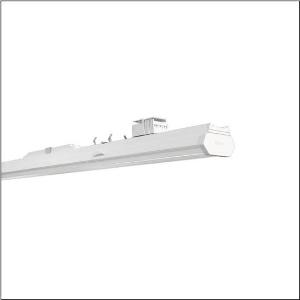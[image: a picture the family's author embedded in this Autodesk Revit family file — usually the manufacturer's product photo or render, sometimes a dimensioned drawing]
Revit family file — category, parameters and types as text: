
# Revit family: licross_r__21_protected_mo_52td11dn4a5g_03df
name_source: partatom
category: Lighting Fixtures
units: mm (PartAtom-declared; Revit-internal decimal feet)

## family parameters
Cut with Voids When Loaded = No
Host = Face
Light Source = No
Part Type = Normal
Room Calculation Point = No
Round Connector Dimension = Use Diameter
Shared = No

## types (1)
- --- (1 x LED, 10650 lm, 62 W, 4000K)
    Apparent Load = 62 VA
    CIE Flux Codes = 83 94 98 100 100
    Color Rendering = 80
    Color Temperature = 4000K
    Default Elevation = 1800 mm
    Description = Licross® 21 Protected MO, luminaire insert, of sheet steel, galvanised, coil coated, white, length: 1.500mm, width: 90mm, height: 103mm, LED rated luminous flux: 10.650lm, light colour: 840, control gear: DALI 2, with plug, 5-pole, with phase selection, mains connection: 220..240V, AC, 50/60Hz, rated input power: 62W, halogen-free wiring, primary light control with lens, of plastic, primary optical cover: cover, of PMMA, light emission: direct distribution, primary light characteristic: symmetric, protection rating (complete): IP54, insulation class (complete): insulation class I (protective earthing), certification: CE, ENEC, VDE, UKCA, protection symbol: D if used in an environment with non-conductive dust loads with corresponding accessories, impact resistance: IK06, permissible ambient temperature for indoor applications: -25..+35°C, corresponds to IFS (International Featured Standards) requirements for safety and quality in the food industry, reducing of maximum allowable ambient temperature of 5°C with ceiling mounting, LABS conformity tested according to VDMA 24364:2018-05, packaging unit: 1 piece
    Height = 92 mm
    Lamp = 1 x LED
    Lamp Light Flux = 10650 lm
    Lamp Power = 62 W
    Lamp count = 1
    Length = 1500 mm
    Luminous efficacy = 172 lm/W
    Manufacturer = Siteco
    ModVariant = No
    Model = 52TD11DN4A5G
    Mounting Place = Ceiling
    Mounting Type = Pendant
    Number of Poles = 1
    OnlyDefault = Yes
    Power Factor = 1
    Product Name = Licross® 21 Protected MO
    Product group = luminaire insert
    ProductGroupID = 901
    Protection Class = Protection class I
    Protection Degree = IP 54
    RLX_Detail_Level = 1
    RLX_Emergency_Light_Flux = 0 lm
    RLX_Emergency_Type = 0
    RLX_Emergency_Type_DB = No
    RlxData = <blob elided: 24201 chars, md5=10d247ae>
    Socket = socket
    Standby Power = 0 W
    System Light Flux = 10650 lm
    System Power = 62 W
    Type Comments = factory setting: luminous flux: 100 % | dim-lin: 254 | 418 mA
    Type Image = l_1256148.jpg
    URL = http://relux.com
    VarID = @adj_077993
    Voltage = 0 V
    Weight = 0.00 kg
    Width = 88 mm

## geometry (parser evidence)
native form markers: Blend x4, Sweep x11
no freeform markers — native parametric forms only
